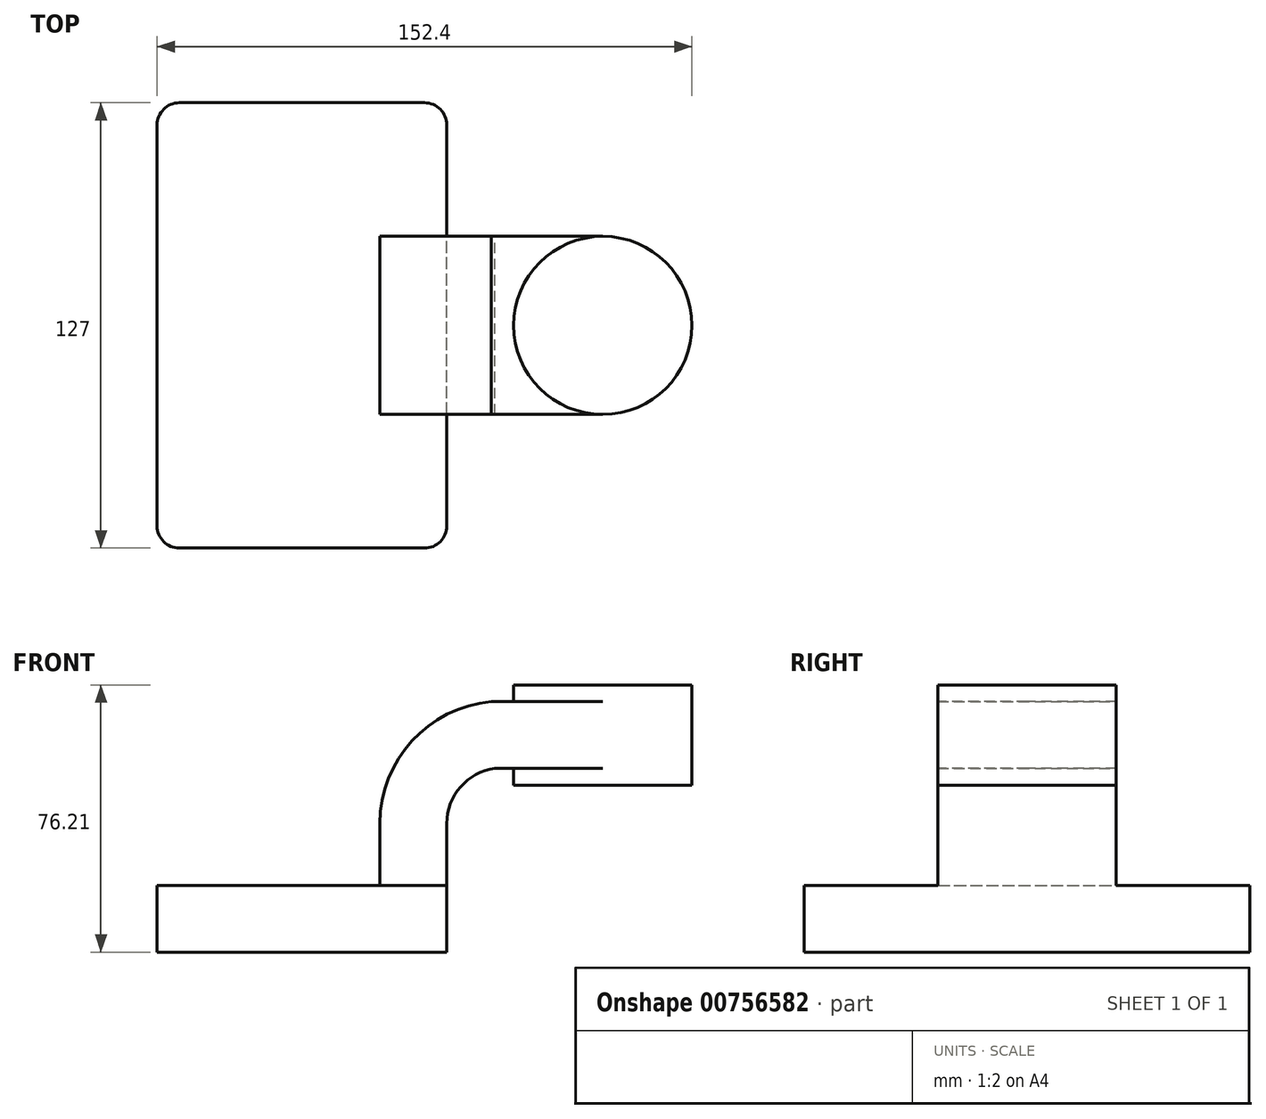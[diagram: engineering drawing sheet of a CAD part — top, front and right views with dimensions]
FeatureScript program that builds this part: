
annotation { "Feature Type Name" : "Feature", "Feature Type Description" : "" }
export const myFeature = defineFeature(function(context is Context, id is Id, definition is map)
    precondition{}
    {
        {
            var Q0;
            Q0=qCreatedBy(makeId("Front.planeOp"),FACE);
            var sketch = newSketch(context, id + "F0", { "sketchPlane" : qUnion([Q0])});
            skLineSegment(sketch, "E0.bottom", {"start": v(-41.28, 9.52) * mm, "end": v(41.27, 9.53) * mm});
            skLineSegment(sketch, "E0.top", {"start": v(-41.28, -9.53) * mm, "end": v(41.28, -9.53) * mm});
            skLineSegment(sketch, "E0.left", {"start": v(-41.28, 9.52) * mm, "end": v(-41.27, -9.53) * mm});
            skLineSegment(sketch, "E0.right", {"start": v(41.28, 9.53) * mm, "end": v(41.28, -9.52) * mm});
            skPoint(sketch, "E0.middle", {"position": v(0, 0) * mm});
            skLineSegment(sketch, "E1.bottom", {"start": v(60.32, 38.1) * mm, "end": v(111.12, 38.1) * mm});
            skLineSegment(sketch, "E1.top", {"start": v(60.32, 66.67) * mm, "end": v(111.12, 66.67) * mm});
            skLineSegment(sketch, "E1.left", {"start": v(60.32, 38.1) * mm, "end": v(60.32, 66.67) * mm});
            skLineSegment(sketch, "E1.right", {"start": v(111.12, 38.1) * mm, "end": v(111.12, 66.67) * mm});
            skPoint(sketch, "E1.middle", {"position": v(85.72, 52.39) * mm});
            skLineSegment(sketch, "E2", {"start": v(41.27, 9.53) * mm, "end": v(41.27, 27.15) * mm});
            skArc(sketch, "E3", {"start": v(41.27, 27.15) * mm, "mid": v(45.2, 37.59) * mm, "end": v(55, 42.88) * mm});
            skLineSegment(sketch, "E4", {"start": v(55, 42.88) * mm, "end": v(85.72, 42.88) * mm});
            skLineSegment(sketch, "E5.0", {"start": v(53.97, 61.93) * mm, "end": v(85.72, 61.93) * mm});
            skArc(sketch, "E5.1", {"start": v(22.22, 27.15) * mm, "mid": v(31.35, 50.69) * mm, "end": v(53.97, 61.93) * mm});
            skLineSegment(sketch, "E5.2", {"start": v(22.22, 9.53) * mm, "end": v(22.22, 27.15) * mm});
            skLineSegment(sketch, "E6", {"start": v(85.72, 38.1) * mm, "end": v(85.72, 66.67) * mm});
            skFitSpline(sketch, "E7", {"points": [v(-41.28, 9.52) * mm, v(53.97, 61.93) * mm], "startDerivative": vector(-0.15, 78.6) * mm, "endDerivative": vector(122.64, 2.33) * mm});
            skSolve(sketch);
        }
        {
            var Q0;
            Q0=makeQuery(id+"F0.imprint","IMPRINT",FACE,{"disambiguationData":[TD([[makeQuery(id+"F0.imprint","IMPRINT",EDGE,{"derivedFrom":sQuery(id+"F0.wireOp",EDGE,"E0.top")}),1.0]])]});
            extrude(context, id + "F1", {"entities" : qUnion([Q0]), "endBound" : BoundingType.SYMMETRIC, "depth" : 127 * mm, "offsetDistance" : 25.4 * mm});
        }
        {
            var Q0;
            {var subQ0=sQuery(id+"F0.wireOp",EDGE,"E4");var subQ1=sQuery(id+"F0.wireOp",EDGE,"E1.left");var subQ2=makeQuery(id+"F0.imprint","INTERSECT",VERTEX,{"derivedFrom":[subQ1,subQ0]});Q0=makeQuery(id+"F0.imprint","IMPRINT",FACE,{"disambiguationData":[TD([[makeQuery(id+"F0.imprint","IMPRINT",EDGE,{"disambiguationData":[TD([[subQ2,-1.0]])],"derivedFrom":subQ1}),-1.0]])]});}
            var Q1;
            {var subQ1=sQuery(id+"F0.wireOp",EDGE,"E2");Q1=makeQuery(id+"F0.imprint","IMPRINT",FACE,{"disambiguationData":[TD([[makeQuery(id+"F0.imprint","IMPRINT",EDGE,{"derivedFrom":subQ1}),1.0]])]});}
            extrude(context, id + "F2", {"entities" : qUnion([Q0, Q1]), "operationType" : NewBodyOperationType.ADD, "endBound" : BoundingType.SYMMETRIC, "depth" : 50.8 * mm, "offsetDistance" : 25.4 * mm});
        }
        {
            var Q0;
            Q0=makeQuery(id+"F0.imprint","IMPRINT",FACE,{"disambiguationData":[TD([[makeQuery(id+"F0.imprint","IMPRINT",EDGE,{"derivedFrom":sQuery(id+"F0.wireOp",EDGE,"E5.1")}),1.0]])]});
            extrude(context, id + "F3", {"entities" : qUnion([Q0]), "operationType" : NewBodyOperationType.ADD, "endBound" : BoundingType.SYMMETRIC, "depth" : 15.88 * mm, "offsetDistance" : 25.4 * mm});
        }
        {
            var Q0;
            {var subQ0=sQuery(id+"F0.wireOp",EDGE,"E1.right");Q0=makeQuery(id+"F0.imprint","IMPRINT",FACE,{"disambiguationData":[TD([[makeQuery(id+"F0.imprint","IMPRINT",EDGE,{"derivedFrom":subQ0}),1.0]])]});}
            var Q1;
            Q1=sQuery(id+"F0.wireOp",EDGE,"E6");
            revolve(context, id + "F4", {"operationType" : NewBodyOperationType.ADD, "surfaceOperationType" : NewSurfaceOperationType.NEW, "entities" : qUnion([Q0]), "axis" : qUnion([Q1]), "revolveType" : RevolveType.FULL});
        }
        {
            var Q0;
            Q0=makeQuery(id+"F1.opExtrude","CAP_EDGE",EDGE,{"disambiguationData":[OSD([sQuery(id+"F0.wireOp",EDGE,"E0.right")])],"isStart":false});
            var Q1;
            Q1=makeQuery(id+"F1.opExtrude","CAP_EDGE",EDGE,{"disambiguationData":[OSD([sQuery(id+"F0.wireOp",EDGE,"E0.left")])],"isStart":false});
            var Q2;
            Q2=makeQuery(id+"F1.opExtrude","CAP_EDGE",EDGE,{"disambiguationData":[OSD([sQuery(id+"F0.wireOp",EDGE,"E0.right")])],"isStart":true});
            var Q3;
            Q3=makeQuery(id+"F1.opExtrude","CAP_EDGE",EDGE,{"disambiguationData":[OSD([sQuery(id+"F0.wireOp",EDGE,"E0.left")])],"isStart":true});
            fillet(context, id + "F5", {"entities" : qUnion([Q0, Q1, Q2, Q3]), "radius" : 6.35 * mm, "tangentPropagation" : true, "allowEdgeOverflow" : false});
        }
    });
